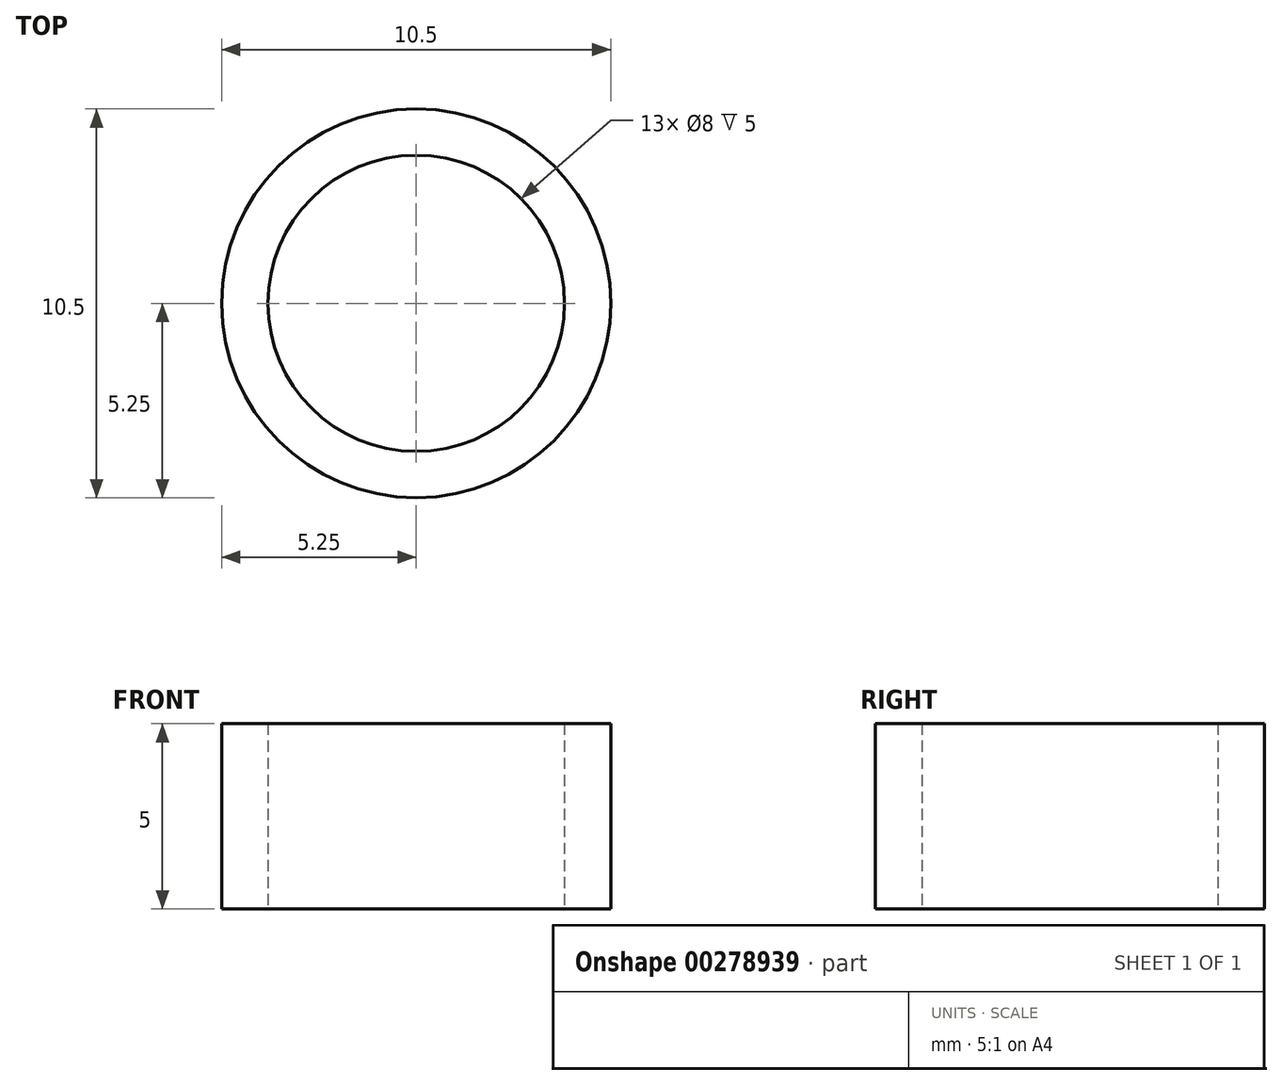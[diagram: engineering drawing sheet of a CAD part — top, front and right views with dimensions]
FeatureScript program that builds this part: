
annotation { "Feature Type Name" : "Feature", "Feature Type Description" : "" }
export const myFeature = defineFeature(function(context is Context, id is Id, definition is map)
    precondition{}
    {
        {
            var Q0;
            Q0=qCreatedBy(makeId("Top.planeOp"),FACE);
            var sketch = newSketch(context, id + "F0", { "sketchPlane" : qUnion([Q0])});
            skCircle(sketch, "E0", {"center": v(0, 0) * mm, "radius": 5.25 * mm});
            skCircle(sketch, "E1", {"center": v(0, 0) * mm, "radius": 4 * mm});
            skSolve(sketch);
        }
        {
            var Q0;
            Q0=makeQuery(id+"F0.imprint","IMPRINT",FACE,{"disambiguationData":[TD([[makeQuery(id+"F0.imprint","IMPRINT",EDGE,{"derivedFrom":sQuery(id+"F0.wireOp",EDGE,"E0")}),1.0]])]});
            extrude(context, id + "F1", {"entities" : qUnion([Q0]), "depth" : 5 * mm});
        }
    });
